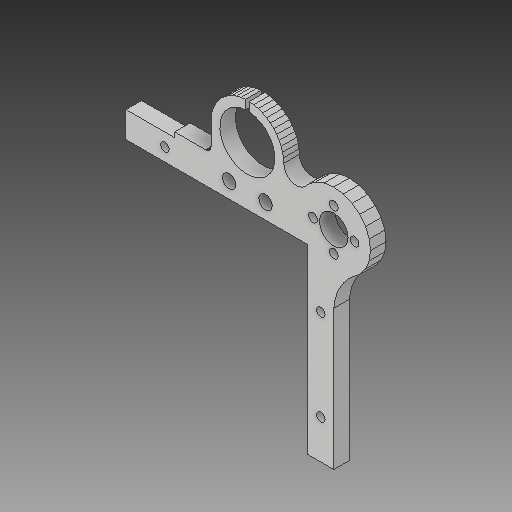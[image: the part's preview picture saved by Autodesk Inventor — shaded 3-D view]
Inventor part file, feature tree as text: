
AUTODESK INVENTOR PART (.ipt)
format: ipt  version: 2018 (Build 220112000, 112)  size: 449,024 bytes
history: native  units: mm
features: sketch x4, hole x3, extrude x1
ambient origin geometry x8: Origin, YZ Plane, XZ Plane, XY Plane, X Axis, Y Axis, Z Axis, Center Point
bodies: Solid1 (feature_tree)
feature tree (8):
  extrude  "Extrusion1"  [1 undecoded]
  hole  "Hole1"  [1 undecoded]
  hole  "Hole2"  [1 undecoded]
  hole  "Hole3"  [1 undecoded]
  sketch  "Sketch1"  dims[d0=6.0mm d1=0.0mm]
  sketch  "Sketch2"  dims[d2=3.3mm d3=6.0mm d4=4.0mm d5=2.0mm d6=90.0deg d7=8.0mm d8=20.594885mm]
  sketch  "Sketch3"  dims[d9=3.4mm d10=6.0mm d11=4.0mm d12=2.0mm d13=90.0deg d14=8.0mm d15=20.594885mm]
  sketch  "Sketch4"  dims[d16=21.2mm d17=6.0mm d18=4.0mm d19=2.0mm d20=90.0deg d21=8.0mm d22=20.594885mm]
note: 4 required parameter values undecoded (feature->parameter linkage not recoverable at this tier; creation-order binding heuristic only, values carry confidence <= 0.55)
